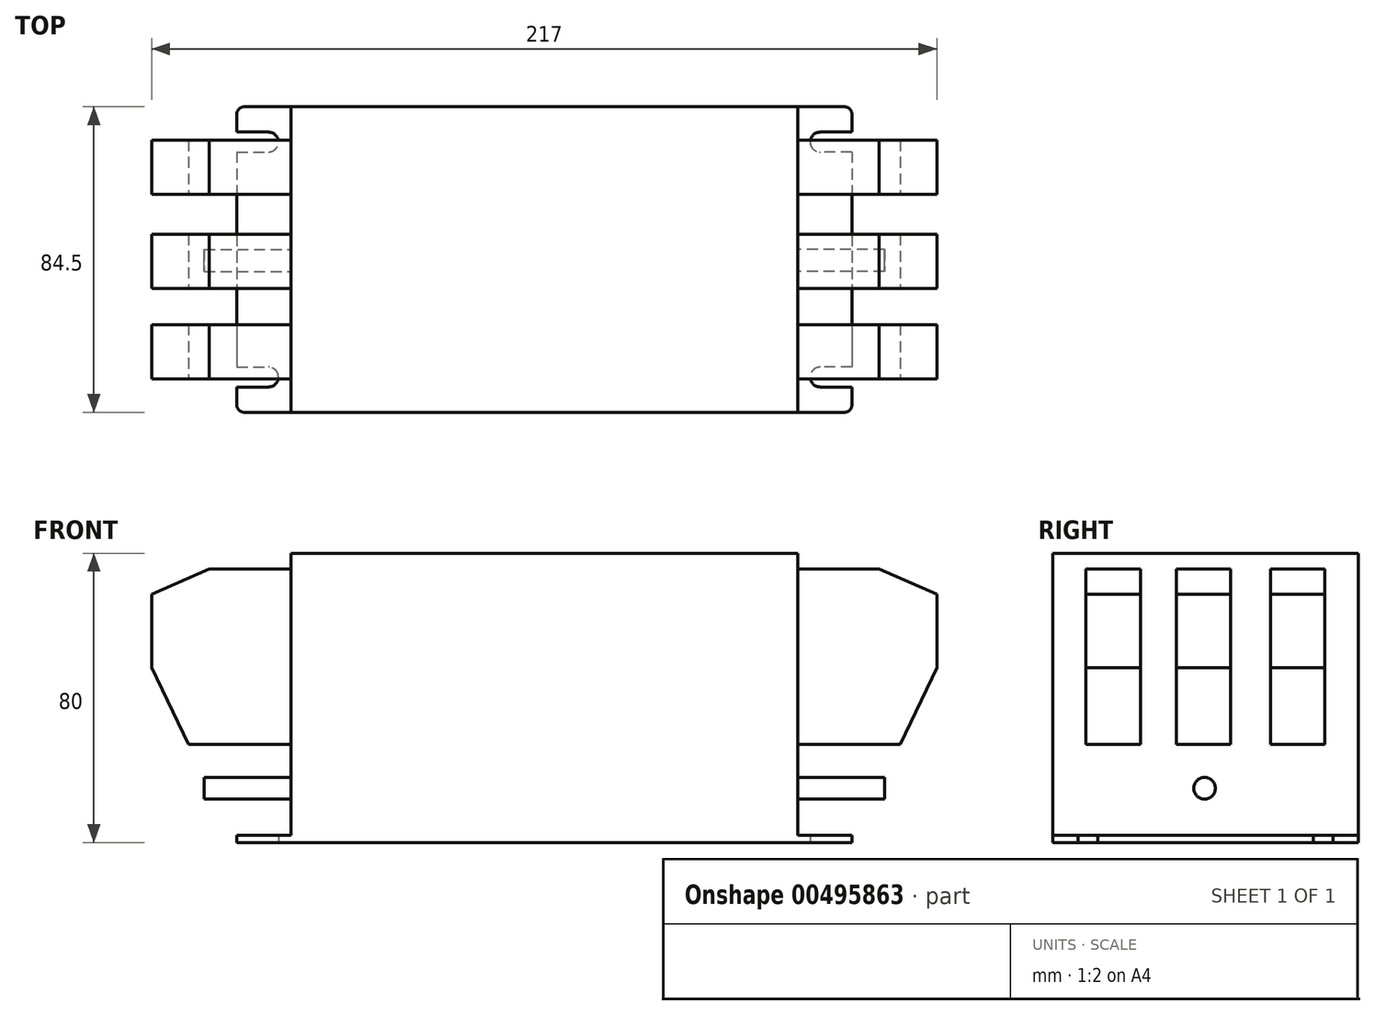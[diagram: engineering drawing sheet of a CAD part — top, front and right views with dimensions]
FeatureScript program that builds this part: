
annotation { "Feature Type Name" : "Feature", "Feature Type Description" : "" }
export const myFeature = defineFeature(function(context is Context, id is Id, definition is map)
    precondition{}
    {
        {
            var Q0;
            Q0=qCreatedBy(makeId("Top.planeOp"),FACE);
            var sketch = newSketch(context, id + "F0", { "sketchPlane" : qUnion([Q0])});
            skLineSegment(sketch, "E0.bottom", {"start": v(83, 42.25) * mm, "end": v(-83, 42.25) * mm});
            skLineSegment(sketch, "E0.top", {"start": v(83, -42.25) * mm, "end": v(-83, -42.25) * mm});
            skLineSegment(sketch, "E0.left", {"start": v(85, 40.25) * mm, "end": v(85, 35.25) * mm});
            skLineSegment(sketch, "E0.right", {"start": v(-85, 40.25) * mm, "end": v(-85, 35.25) * mm});
            skPoint(sketch, "E0.middle", {"position": v(0, 0) * mm});
            skLineSegment(sketch, "E1", {"start": v(-85, 35.25) * mm, "end": v(-76.25, 35.25) * mm});
            skLineSegment(sketch, "E2", {"start": v(-85, 29.75) * mm, "end": v(-76.25, 29.75) * mm});
            skArc(sketch, "E3", {"start": v(-76.25, 35.25) * mm, "mid": v(-73.5, 32.5) * mm, "end": v(-76.25, 29.75) * mm});
            skLineSegment(sketch, "E4.MirrorCS", {"start": v(-85, -35.25) * mm, "end": v(-76.25, -35.25) * mm});
            skLineSegment(sketch, "E5.MirrorCS", {"start": v(-85, -29.75) * mm, "end": v(-76.25, -29.75) * mm});
            skArc(sketch, "E6.MirrorCS", {"start": v(-76.25, -35.25) * mm, "mid": v(-73.5, -32.5) * mm, "end": v(-76.25, -29.75) * mm});
            skLineSegment(sketch, "E7.MirrorCS", {"start": v(85, -35.25) * mm, "end": v(76.25, -35.25) * mm});
            skArc(sketch, "E8.MirrorCS", {"start": v(76.25, -35.25) * mm, "mid": v(73.5, -32.5) * mm, "end": v(76.25, -29.75) * mm});
            skLineSegment(sketch, "E9.MirrorCS", {"start": v(85, -29.75) * mm, "end": v(76.25, -29.75) * mm});
            skLineSegment(sketch, "E10.MirrorCS", {"start": v(85, 35.25) * mm, "end": v(76.25, 35.25) * mm});
            skLineSegment(sketch, "E11.MirrorCS", {"start": v(85, 29.75) * mm, "end": v(76.25, 29.75) * mm});
            skArc(sketch, "E12.MirrorCS", {"start": v(76.25, 35.25) * mm, "mid": v(73.5, 32.5) * mm, "end": v(76.25, 29.75) * mm});
            skPoint(sketch, "E13.visualSharp", {"position": v(-85, 42.25) * mm});
            skArc(sketch, "E13.filletArc", {"start": v(-83, 42.25) * mm, "mid": v(-84.41, 41.66) * mm, "end": v(-85, 40.25) * mm});
            skPoint(sketch, "E14.visualSharp", {"position": v(85, 42.25) * mm});
            skArc(sketch, "E14.filletArc", {"start": v(85, 40.25) * mm, "mid": v(84.41, 41.66) * mm, "end": v(83, 42.25) * mm});
            skPoint(sketch, "E15.visualSharp", {"position": v(85, -42.25) * mm});
            skArc(sketch, "E15.filletArc", {"start": v(83, -42.25) * mm, "mid": v(84.41, -41.66) * mm, "end": v(85, -40.25) * mm});
            skPoint(sketch, "E16.visualSharp", {"position": v(-85, -42.25) * mm});
            skArc(sketch, "E16.filletArc", {"start": v(-85, -40.25) * mm, "mid": v(-84.41, -41.66) * mm, "end": v(-83, -42.25) * mm});
            skLineSegment(sketch, "E17.trimOffspring", {"start": v(85, 29.75) * mm, "end": v(85, -29.75) * mm});
            skLineSegment(sketch, "E18.trimOffspring", {"start": v(85, -35.25) * mm, "end": v(85, -40.25) * mm});
            skLineSegment(sketch, "E19.trimOffspring", {"start": v(-85, 29.75) * mm, "end": v(-85, -29.75) * mm});
            skLineSegment(sketch, "E20.trimOffspring", {"start": v(-85, -35.25) * mm, "end": v(-85, -40.25) * mm});
            skSolve(sketch);
        }
        {
            var Q0;
            Q0=qSketchRegion(id+"F0",true);
            extrude(context, id + "F1", {"entities" : qUnion([Q0]), "depth" : 2 * mm});
        }
        {
            var Q0;
            Q0=makeQuery(id+"F1.opExtrude","CAP_FACE",FACE,{"disambiguationData":[OSD([sQuery(id+"F0.wireOp",EDGE,"E0.bottom"),sQuery(id+"F0.wireOp",EDGE,"E0.top"),sQuery(id+"F0.wireOp",EDGE,"E0.left"),sQuery(id+"F0.wireOp",EDGE,"E0.right"),sQuery(id+"F0.wireOp",EDGE,"E1"),sQuery(id+"F0.wireOp",EDGE,"E2"),sQuery(id+"F0.wireOp",EDGE,"E3"),sQuery(id+"F0.wireOp",EDGE,"E6.MirrorCS"),sQuery(id+"F0.wireOp",EDGE,"E5.MirrorCS"),sQuery(id+"F0.wireOp",EDGE,"E4.MirrorCS"),sQuery(id+"F0.wireOp",EDGE,"E7.MirrorCS"),sQuery(id+"F0.wireOp",EDGE,"E8.MirrorCS"),sQuery(id+"F0.wireOp",EDGE,"E9.MirrorCS"),sQuery(id+"F0.wireOp",EDGE,"E10.MirrorCS"),sQuery(id+"F0.wireOp",EDGE,"E11.MirrorCS"),sQuery(id+"F0.wireOp",EDGE,"E12.MirrorCS"),sQuery(id+"F0.wireOp",EDGE,"E13.filletArc"),sQuery(id+"F0.wireOp",EDGE,"E14.filletArc"),sQuery(id+"F0.wireOp",EDGE,"E15.filletArc"),sQuery(id+"F0.wireOp",EDGE,"E16.filletArc"),sQuery(id+"F0.wireOp",EDGE,"E17.trimOffspring"),sQuery(id+"F0.wireOp",EDGE,"E18.trimOffspring"),sQuery(id+"F0.wireOp",EDGE,"E19.trimOffspring"),sQuery(id+"F0.wireOp",EDGE,"E20.trimOffspring")])],"isStart":false});
            var sketch = newSketch(context, id + "F2", { "sketchPlane" : qUnion([Q0])});
            skLineSegment(sketch, "E21.bottom", {"start": v(70, 42.25) * mm, "end": v(-70, 42.25) * mm});
            skLineSegment(sketch, "E21.top", {"start": v(70, -42.25) * mm, "end": v(-70, -42.25) * mm});
            skLineSegment(sketch, "E21.left", {"start": v(70, 42.25) * mm, "end": v(70, -42.25) * mm});
            skLineSegment(sketch, "E21.right", {"start": v(-70, 42.25) * mm, "end": v(-70, -42.25) * mm});
            skPoint(sketch, "E21.middle", {"position": v(0, 0) * mm});
            skSolve(sketch);
        }
        {
            var Q0;
            Q0=qSketchRegion(id+"F2",true);
            extrude(context, id + "F3", {"entities" : qUnion([Q0]), "operationType" : NewBodyOperationType.ADD, "depth" : 78 * mm});
        }
        {
            var Q0;
            Q0=makeQuery(id+"F3.opExtrude","SWEPT_FACE",FACE,{"disambiguationData":[OSD([sQuery(id+"F2.wireOp",EDGE,"E21.right")])]});
            var sketch = newSketch(context, id + "F4", { "sketchPlane" : qUnion([Q0])});
            skLineSegment(sketch, "E22.bottom", {"start": v(-33, 75.7) * mm, "end": v(-18, 75.7) * mm});
            skLineSegment(sketch, "E22.top", {"start": v(-33, 27.2) * mm, "end": v(-18, 27.2) * mm});
            skLineSegment(sketch, "E22.left", {"start": v(-33, 75.7) * mm, "end": v(-33, 27.2) * mm});
            skLineSegment(sketch, "E22.right", {"start": v(-18, 75.7) * mm, "end": v(-18, 27.2) * mm});
            skLineSegment(sketch, "E23.bottom", {"start": v(-7, 75.7) * mm, "end": v(8, 75.7) * mm});
            skLineSegment(sketch, "E23.top", {"start": v(-7, 27.2) * mm, "end": v(8, 27.2) * mm});
            skLineSegment(sketch, "E23.left", {"start": v(-7, 75.7) * mm, "end": v(-7, 27.2) * mm});
            skLineSegment(sketch, "E23.right", {"start": v(8, 75.7) * mm, "end": v(8, 27.2) * mm});
            skLineSegment(sketch, "E24.MirrorCS", {"start": v(18, 75.7) * mm, "end": v(18, 27.2) * mm});
            skLineSegment(sketch, "E25.MirrorCS", {"start": v(33, 75.7) * mm, "end": v(33, 27.2) * mm});
            skLineSegment(sketch, "E26.MirrorCS", {"start": v(7, 75.7) * mm, "end": v(-8, 75.7) * mm});
            skLineSegment(sketch, "E27.MirrorCS", {"start": v(7, 27.2) * mm, "end": v(-8, 27.2) * mm});
            skLineSegment(sketch, "E28.MirrorCS", {"start": v(33, 27.2) * mm, "end": v(18, 27.2) * mm});
            skLineSegment(sketch, "E29.MirrorCS", {"start": v(33, 75.7) * mm, "end": v(18, 75.7) * mm});
            skLineSegment(sketch, "E30", {"start": v(-42.25, 27.2) * mm, "end": v(42.25, 27.2) * mm, "construction": true});
            skLineSegment(sketch, "E31", {"start": v(-42.25, 75.7) * mm, "end": v(42.25, 75.7) * mm, "construction": true});
            skSolve(sketch);
        }
        {
            var Q0;
            Q0=qSketchRegion(id+"F4",true);
            extrude(context, id + "F5", {"entities" : qUnion([Q0]), "depth" : ((217 - 140) / 2) * mm});
        }
        {
            var Q0;
            Q0=makeQuery(id+"F5.opExtrude","SWEPT_FACE",FACE,{"disambiguationData":[OSD([sQuery(id+"F4.wireOp",EDGE,"E25.MirrorCS")])]});
            var sketch = newSketch(context, id + "F6", { "sketchPlane" : qUnion([Q0])});
            skLineSegment(sketch, "E32", {"start": v(-108.5, 68.62) * mm, "end": v(-92.58, 75.7) * mm});
            skLineSegment(sketch, "E33", {"start": v(-92.58, 75.7) * mm, "end": v(-156.8, 106.62) * mm});
            skLineSegment(sketch, "E34", {"start": v(-156.8, 106.62) * mm, "end": v(-183.46, 103.24) * mm});
            skLineSegment(sketch, "E35", {"start": v(-108.5, 68.62) * mm, "end": v(-108.5, 48.3) * mm});
            skLineSegment(sketch, "E36", {"start": v(-108.5, 48.3) * mm, "end": v(-98.38, 27.2) * mm});
            skLineSegment(sketch, "E37", {"start": v(-98.38, 27.2) * mm, "end": v(-183.46, 0) * mm});
            skLineSegment(sketch, "E38", {"start": v(-183.46, 0) * mm, "end": v(-183.46, 103.24) * mm});
            skPoint(sketch, "E39", {"position": v(-89.25, 75.7) * mm});
            skPoint(sketch, "E40", {"position": v(-108.5, 51.45) * mm});
            skSolve(sketch);
        }
        {
            var Q0;
            Q0=qSketchRegion(id+"F6",true);
            extrude(context, id + "F7", {"entities" : qUnion([Q0]), "operationType" : NewBodyOperationType.REMOVE, "oppositeDirection" : true, "depth" : 200 * mm});
        }
        {
            var Q0;
            Q0=makeQuery(id+"F3.opExtrude","SWEPT_FACE",FACE,{"disambiguationData":[OSD([sQuery(id+"F2.wireOp",EDGE,"E21.right")])]});
            var sketch = newSketch(context, id + "F8", { "sketchPlane" : qUnion([Q0])});
            skCircle(sketch, "E41", {"center": v(0.25, 15) * mm, "radius": 3 * mm});
            skSolve(sketch);
        }
        {
            var Q0;
            Q0=qSketchRegion(id+"F8",true);
            extrude(context, id + "F9", {"entities" : qUnion([Q0]), "depth" : 24 * mm});
        }
        {
            var Q0;
            Q0=makeQuery(id+"F5.opExtrude","SWEPT_BODY",BODY,{"disambiguationData":[OSD([sQuery(id+"F4.wireOp",EDGE,"E22.bottom"),sQuery(id+"F4.wireOp",EDGE,"E22.top"),sQuery(id+"F4.wireOp",EDGE,"E22.left"),sQuery(id+"F4.wireOp",EDGE,"E22.right")])]});
            var Q1;
            Q1=makeQuery(id+"F5.opExtrude","SWEPT_BODY",BODY,{"disambiguationData":[OSD([sQuery(id+"F4.wireOp",EDGE,"E23.bottom"),sQuery(id+"F4.wireOp",EDGE,"E23.top"),sQuery(id+"F4.wireOp",EDGE,"E23.left"),sQuery(id+"F4.wireOp",EDGE,"E23.right")])]});
            var Q2;
            Q2=makeQuery(id+"F5.opExtrude","SWEPT_BODY",BODY,{"disambiguationData":[OSD([sQuery(id+"F4.wireOp",EDGE,"2c7fa774-8186-412e-95ba-48c3659cf0bb0.MirrorCS"),sQuery(id+"F4.wireOp",EDGE,"e2ad8afa-064d-4086-936c-4bd32b6efbf30.MirrorCS"),sQuery(id+"F4.wireOp",EDGE,"E26.MirrorCS"),sQuery(id+"F4.wireOp",EDGE,"E27.MirrorCS")])]});
            var Q3;
            Q3=makeQuery(id+"F5.opExtrude","SWEPT_BODY",BODY,{"disambiguationData":[OSD([sQuery(id+"F4.wireOp",EDGE,"E24.MirrorCS"),sQuery(id+"F4.wireOp",EDGE,"E25.MirrorCS"),sQuery(id+"F4.wireOp",EDGE,"E28.MirrorCS"),sQuery(id+"F4.wireOp",EDGE,"E29.MirrorCS")])]});
            var Q4;
            Q4=makeQuery(id+"F9.opExtrude","SWEPT_BODY",BODY,{"disambiguationData":[OSD([sQuery(id+"F8.wireOp",EDGE,"E41")])]});
            var Q5;
            Q5=qCreatedBy(makeId("Right.planeOp"),FACE);
            mirror(context, id + "F10", {"entities" : qUnion([Q0, Q1, Q2, Q3, Q4]), "mirrorPlane" : qUnion([Q5])});
        }
    });
